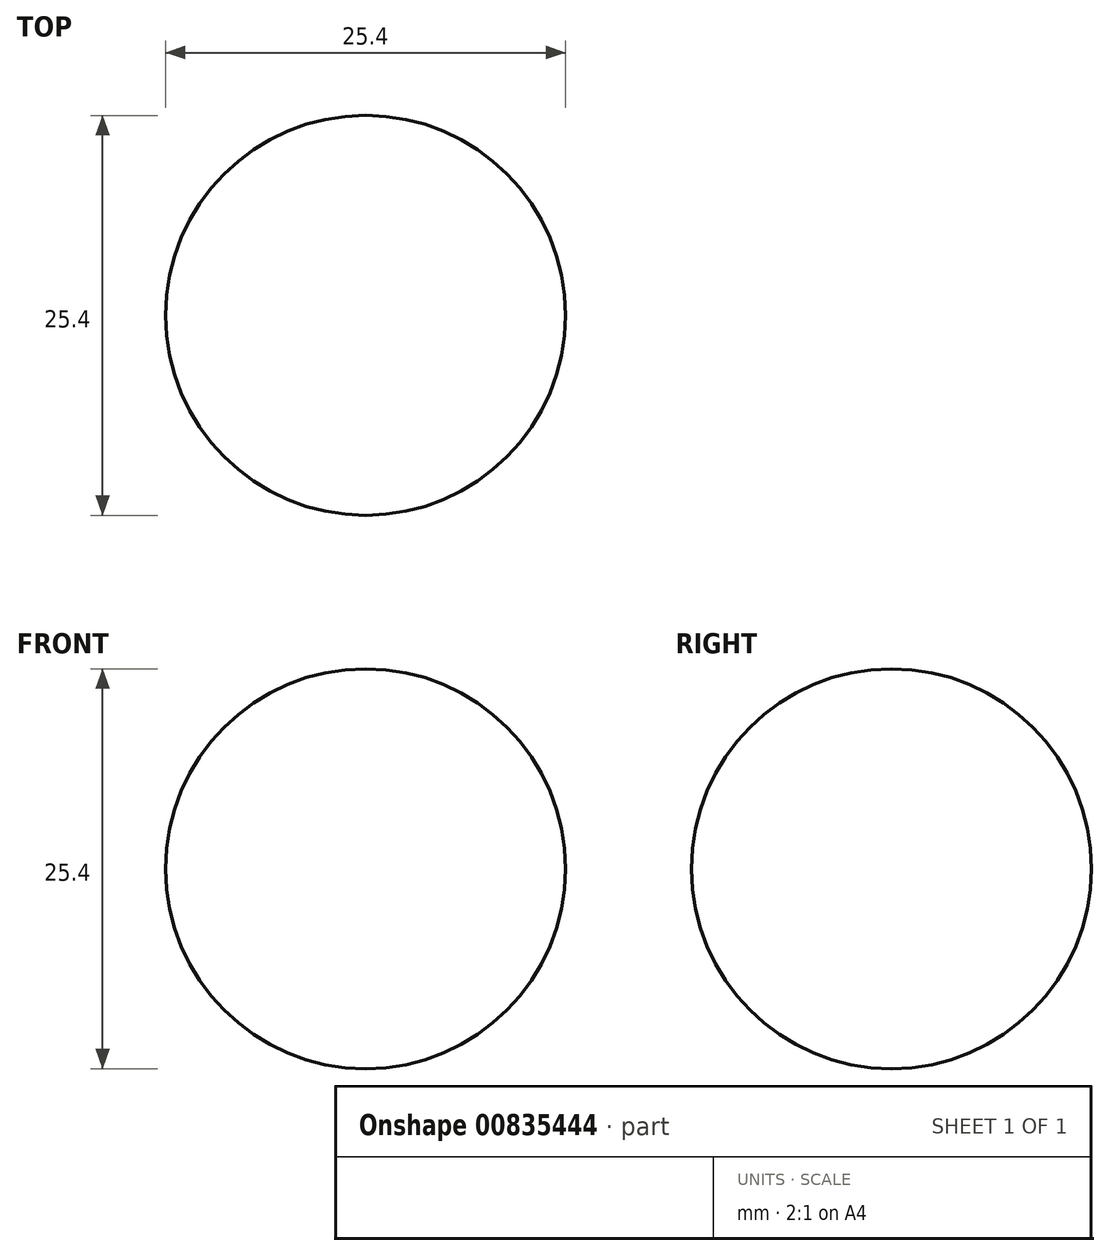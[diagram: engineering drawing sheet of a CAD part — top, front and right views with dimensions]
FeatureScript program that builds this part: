
annotation { "Feature Type Name" : "Feature", "Feature Type Description" : "" }
export const myFeature = defineFeature(function(context is Context, id is Id, definition is map)
    precondition{}
    {
        {
            var Q0;
            Q0=qCreatedBy(makeId("Front.planeOp"),FACE);
            var sketch = newSketch(context, id + "F0", { "sketchPlane" : qUnion([Q0])});
            skCircle(sketch, "E0", {"center": v(0, 0) * mm, "radius": 12.7 * mm});
            skLineSegment(sketch, "E1", {"start": v(0, 0) * mm, "end": v(0, 12.7) * mm});
            skLineSegment(sketch, "E2", {"start": v(0, 0) * mm, "end": v(0, -12.7) * mm});
            skSolve(sketch);
        }
        {
            var Q0;
            {var subQ0=sQuery(id+"F0.wireOp",EDGE,"E1");Q0=makeQuery(id+"F0.imprint","IMPRINT",FACE,{"disambiguationData":[TD([[makeQuery(id+"F0.imprint","IMPRINT",EDGE,{"derivedFrom":subQ0}),-1.0]])]});}
            var Q1;
            Q1=sQuery(id+"F0.wireOp",EDGE,"E1");
            revolve(context, id + "F1", {"surfaceOperationType" : NewSurfaceOperationType.NEW, "entities" : qUnion([Q0]), "axis" : qUnion([Q1]), "revolveType" : RevolveType.FULL});
        }
    });
